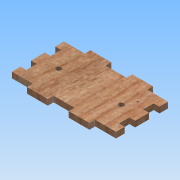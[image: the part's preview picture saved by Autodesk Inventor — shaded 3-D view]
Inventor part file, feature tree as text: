
AUTODESK INVENTOR PART (.ipt)
format: ipt  version: 2015 (Build 190159000, 159)  size: 293,376 bytes
history: native  units: mm
features: other x12, sketch x9, extrude x3, hole x1
ambient origin geometry x8: Origin, YZ Plane, XZ Plane, XY Plane, X Axis, Y Axis, Z Axis, Center Point
bodies: Body1 (feature_tree)
feature tree (25):
  other  "Blocks"
  extrude  "Extrusion2"  Depth=50.0mm
  hole  "Hole5"  [1 undecoded]
  extrude  "Extrusion6"  Depth=20.0mm
  extrude  "Extrusion7"  Depth=5.5mm
  sketch  "Sketch46"  dims[d145=10.0mm]
  sketch  "Sketch47"  dims[d146=8.333333mm d147=5.5mm d148=0.0mm d29=1.0mm d30=1.0mm d116=1.0mm d117=1.0mm]
  sketch  "Sketch44"  dims[d143=0.0mm]
  sketch  "Sketch45"  dims[d144=5.5mm]
  sketch  "Sketch43"  dims[d142=5.5mm]
  sketch  "Sketch10"  dims[d21=100.0mm d22=50.0mm]
  sketch  "Sketch16"  dims[d23=5.5mm d24=0.0mm d52=60.0mm]
  sketch  "Sketch35"  dims[d53=5.0mm d54=6.0mm d55=4.0mm d56=2.0mm d57=90.0deg d58=4.0mm d59=0.0mm d129=20.0mm]
  sketch  "Sketch36"  dims[d130=20.0mm d131=5.5mm]
  other  "Block1"
  other  "Block2"
  other  "Block3"
  other  "Block4"
  other  "Block5"
  other  "Block3:1"
  other  "Block3:2"
  other  "Block4:1"
  other  "Block4:2"
  other  "Block5:1"
  other  "Block5:2"
note: 1 required parameter value undecoded (feature->parameter linkage not recoverable at this tier; creation-order binding heuristic only, values carry confidence <= 0.55)
